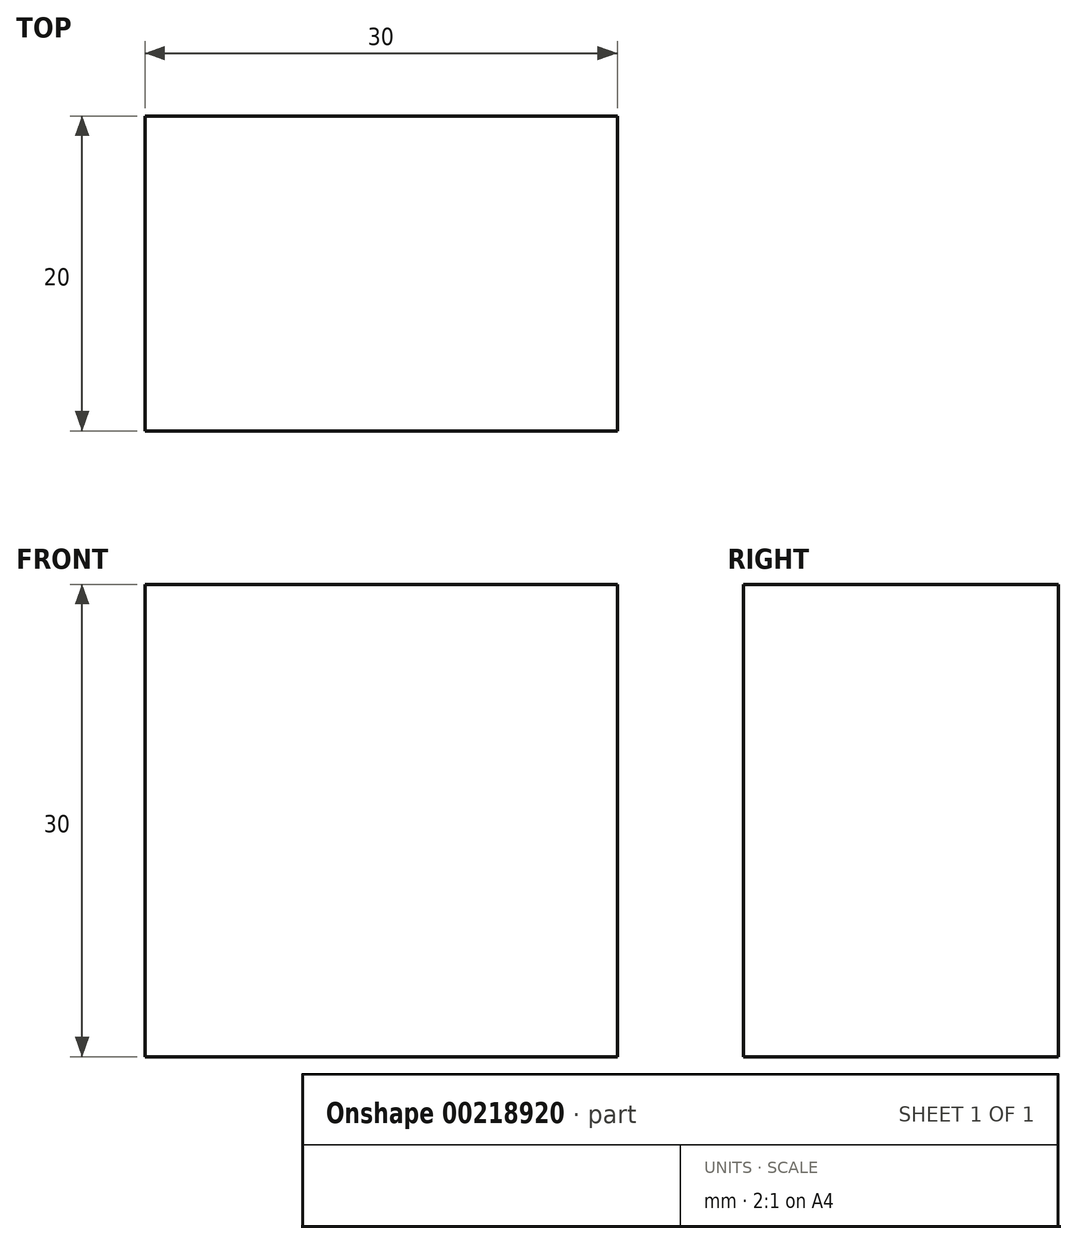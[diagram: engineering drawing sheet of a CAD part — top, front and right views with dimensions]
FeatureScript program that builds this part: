
annotation { "Feature Type Name" : "Feature", "Feature Type Description" : "" }
export const myFeature = defineFeature(function(context is Context, id is Id, definition is map)
    precondition{}
    {
        {
            var Q0;
            Q0=qCreatedBy(makeId("Top.planeOp"),FACE);
            var sketch = newSketch(context, id + "F0", { "sketchPlane" : qUnion([Q0])});
            skLineSegment(sketch, "E0.bottom", {"start": v(-15.42, 5.37) * mm, "end": v(14.58, 5.37) * mm});
            skLineSegment(sketch, "E0.top", {"start": v(-15.42, -14.63) * mm, "end": v(14.58, -14.63) * mm});
            skLineSegment(sketch, "E0.left", {"start": v(-15.42, 5.37) * mm, "end": v(-15.42, -14.63) * mm});
            skLineSegment(sketch, "E0.right", {"start": v(14.58, 5.37) * mm, "end": v(14.58, -14.63) * mm});
            skSolve(sketch);
        }
        {
            var Q0;
            Q0 = qSketchRegion(id + "F0", true);
            extrude(context, id + "F1", {"entities" : qUnion([Q0]), "depth" : 30 * mm, "offsetDistance" : 25 * mm});
        }
    });
